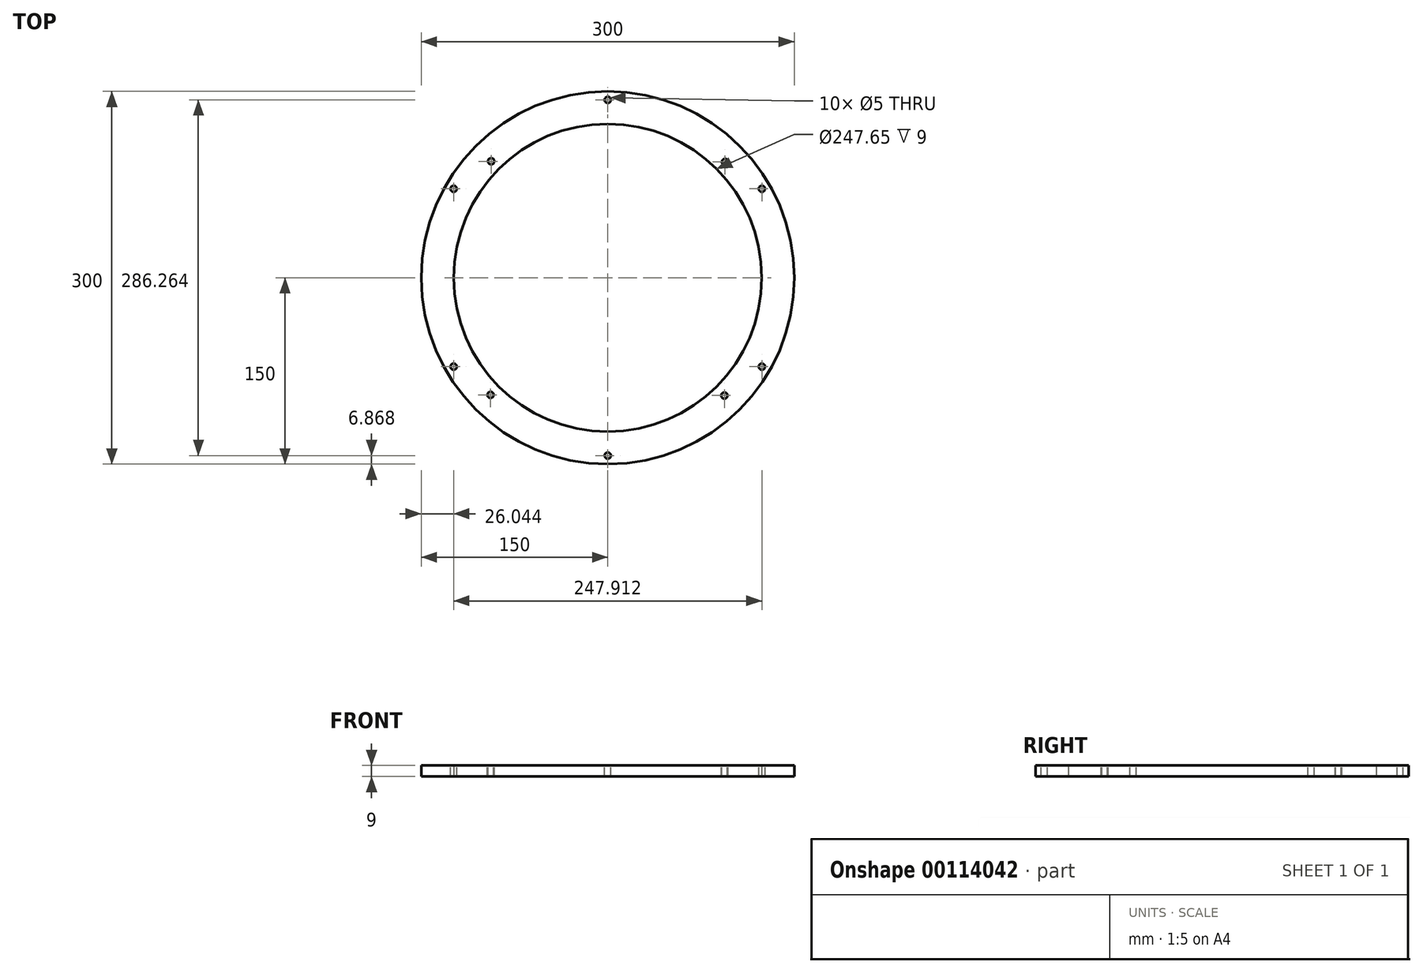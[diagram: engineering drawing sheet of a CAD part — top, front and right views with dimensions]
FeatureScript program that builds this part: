
annotation { "Feature Type Name" : "Feature", "Feature Type Description" : "" }
export const myFeature = defineFeature(function(context is Context, id is Id, definition is map)
    precondition{}
    {
        {
            var Q0;
            Q0=qCreatedBy(makeId("Top.planeOp"),FACE);
            var sketch = newSketch(context, id + "F0", { "sketchPlane" : qUnion([Q0])});
            skCircle(sketch, "E0", {"center": v(0, 0) * mm, "radius": 150 * mm});
            skCircle(sketch, "E1", {"center": v(0, 0) * mm, "radius": 123.83 * mm});
            skSolve(sketch);
        }
        {
            var Q0;
            Q0=makeQuery(id+"F0.imprint","IMPRINT",FACE,{"disambiguationData":[TD([[makeQuery(id+"F0.imprint","IMPRINT",EDGE,{"derivedFrom":sQuery(id+"F0.wireOp",EDGE,"E0")}),1.0]])]});
            extrude(context, id + "F1", {"entities" : qUnion([Q0]), "depth" : 9 * mm});
        }
        {
            var Q0;
            Q0=makeQuery(id+"F1.opExtrude","CAP_FACE",FACE,{"disambiguationData":[OSD([sQuery(id+"F0.wireOp",EDGE,"E0"),sQuery(id+"F0.wireOp",EDGE,"E1")])],"isStart":false});
            var sketch = newSketch(context, id + "F2", { "sketchPlane" : qUnion([Q0])});
            skPoint(sketch, "E2.middle", {"position": v(0, 0) * mm});
            skCircle(sketch, "E3", {"center": v(-94.3, -94.3) * mm, "radius": 2.5 * mm});
            skCircle(sketch, "E4.1.0", {"center": v(93.76, -94.83) * mm, "radius": 2.5 * mm});
            skCircle(sketch, "E4.2.0", {"center": v(94.3, 93.22) * mm, "radius": 2.5 * mm});
            skCircle(sketch, "E4.3.0", {"center": v(-93.76, 93.76) * mm, "radius": 2.5 * mm});
            skPoint(sketch, "E4.center", {"position": v(0, -0.54) * mm});
            skCircle(sketch, "E5", {"center": v(0, 143.13) * mm, "radius": 2.5 * mm});
            skCircle(sketch, "E6.1.0", {"center": v(123.96, 71.57) * mm, "radius": 2.5 * mm});
            skCircle(sketch, "E6.2.0", {"center": v(123.96, -71.57) * mm, "radius": 2.5 * mm});
            skCircle(sketch, "E6.3.0", {"center": v(0, -143.13) * mm, "radius": 2.5 * mm});
            skCircle(sketch, "E6.4.0", {"center": v(-123.96, -71.57) * mm, "radius": 2.5 * mm});
            skCircle(sketch, "E6.5.0", {"center": v(-123.96, 71.57) * mm, "radius": 2.5 * mm});
            skLineSegment(sketch, "E6.anchor1", {"start": v(0, 0) * mm, "end": v(0, 143.13) * mm, "construction": true});
            skLineSegment(sketch, "E6.anchor2", {"start": v(0, 0) * mm, "end": v(-123.96, 71.57) * mm, "construction": true});
            skSolve(sketch);
        }
        {
            var Q0;
            Q0 = qSketchRegion(id + "F2", true);
            extrude(context, id + "F3", {"entities" : qUnion([Q0]), "operationType" : NewBodyOperationType.REMOVE, "oppositeDirection" : true, "depth" : 25.4 * mm});
        }
    });
